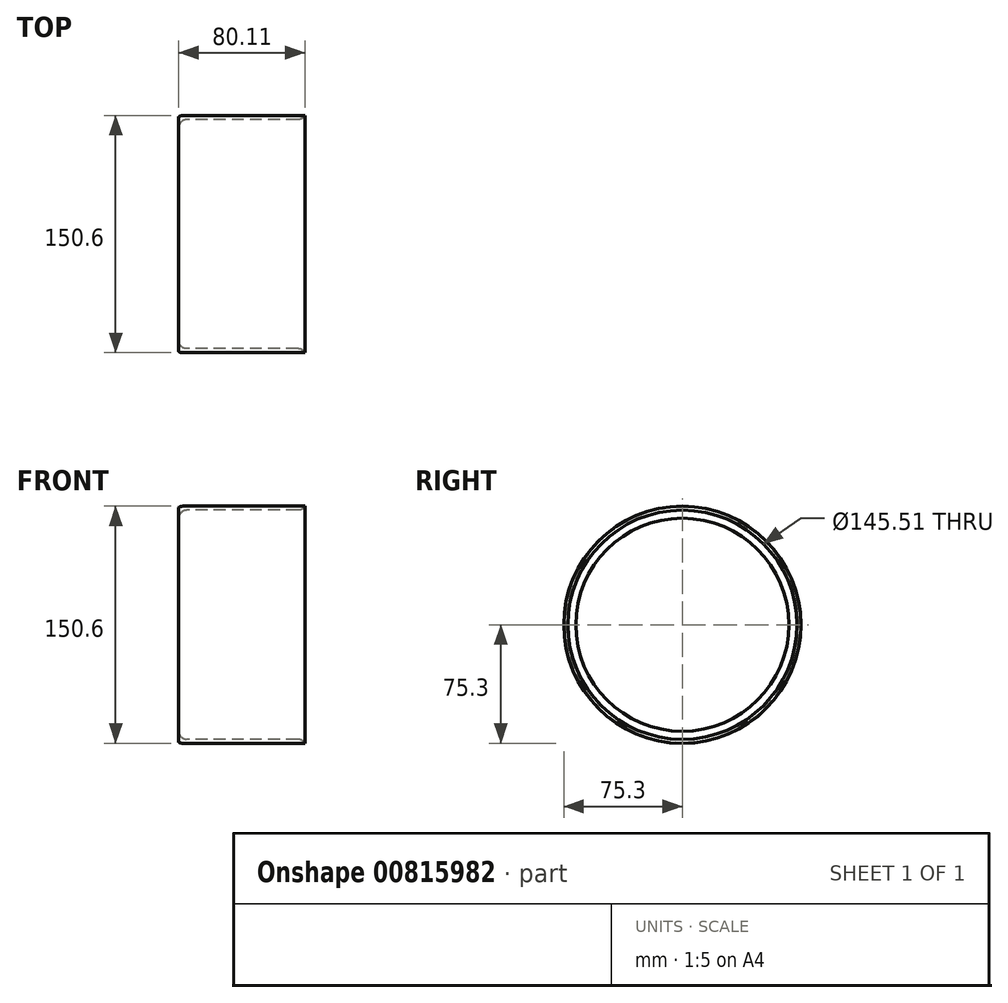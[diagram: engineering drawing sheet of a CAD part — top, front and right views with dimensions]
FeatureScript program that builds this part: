
annotation { "Feature Type Name" : "Feature", "Feature Type Description" : "" }
export const myFeature = defineFeature(function(context is Context, id is Id, definition is map)
    precondition{}
    {
        {
            var Q0;
            Q0=qCreatedBy(makeId("Right.planeOp"),FACE);
            var sketch = newSketch(context, id + "F0", { "sketchPlane" : qUnion([Q0])});
            skCircle(sketch, "E0", {"center": v(0, 0) * mm, "radius": 75.3 * mm});
            skSolve(sketch);
        }
        {
            var Q0;
            Q0=makeQuery(id+"F0.imprint","IMPRINT",FACE,{"disambiguationData":[TD([[makeQuery(id+"F0.imprint","IMPRINT",EDGE,{"derivedFrom":sQuery(id+"F0.wireOp",EDGE,"E0")}),1.0]])]});
            extrude(context, id + "F1", {"entities" : qUnion([Q0]), "depth" : 82.65 * mm, "offsetDistance" : 25.4 * mm});
        }
        {
            var Q0;
            Q0=makeQuery(id+"F1.opExtrude","CAP_FACE",FACE,{"disambiguationData":[OSD([sQuery(id+"F0.wireOp",EDGE,"E0")])],"isStart":false});
            shell(context, id + "F2", {"entities" : qUnion([Q0]), "thickness" : 2.54 * mm});
        }
        {
            var Q0;
            {var subQ0=sQuery(id+"F0.wireOp",EDGE,"E0");Q0=makeQuery(id+"F2.opShell","OFFSET_EDGE",EDGE,{"disambiguationData":[OSD([subQ0]),TDD([makeQuery(id+"F1.opExtrude","CAP_EDGE",EDGE,{"disambiguationData":[OSD([subQ0])],"isStart":false})])]});}
            fillet(context, id + "F3", {"entities" : qUnion([Q0]), "radius" : 5.08 * mm, "tangentPropagation" : true, "allowEdgeOverflow" : false});
        }
        {
            var Q0;
            {var subQ0=sQuery(id+"F0.wireOp",EDGE,"E0");Q0=makeQuery(id+"F2.opShell","OFFSET_FACE",FACE,{"disambiguationData":[OSD([subQ0]),TDD([makeQuery(id+"F1.opExtrude","CAP_FACE",FACE,{"disambiguationData":[OSD([subQ0])],"isStart":true})])]});}
            fillet(context, id + "F4", {"entities" : qUnion([Q0]), "radius" : 5.08 * mm, "tangentPropagation" : true, "allowEdgeOverflow" : false});
        }
        {
            var Q0;
            Q0=makeQuery(id+"F1.opExtrude","CAP_EDGE",EDGE,{"disambiguationData":[OSD([sQuery(id+"F0.wireOp",EDGE,"E0")])],"isStart":true});
            fillet(context, id + "F5", {"entities" : qUnion([Q0]), "radius" : 5.08 * mm, "tangentPropagation" : true, "allowEdgeOverflow" : false});
        }
        {
            var Q0;
            {var subQ0=sQuery(id+"F0.wireOp",EDGE,"E0");Q0=makeQuery(id+"F2.opShell","OFFSET_FACE",FACE,{"disambiguationData":[OSD([subQ0]),TDD([makeQuery(id+"F1.opExtrude","CAP_FACE",FACE,{"disambiguationData":[OSD([subQ0])],"isStart":true})])]});}
            var sketch = newSketch(context, id + "F6", { "sketchPlane" : qUnion([Q0])});
            skPoint(sketch, "E1", {"position": v(0, 0) * mm});
            skSolve(sketch);
        }
        {
            var Q0;
            Q0=sQuery(id+"F6.wireOp",VERTEX,"E1");
            var Q1;
            Q1=makeQuery(id+"F1.opExtrude","SWEPT_BODY",BODY,{"disambiguationData":[OSD([sQuery(id+"F0.wireOp",EDGE,"E0")])]});
            hole(context, id + "F7", {"style" : HoleStyle.SIMPLE, "endStyle" : HoleEndStyle.THROUGH, "holeDiameter" : 635 * mm, "majorDiameter" : 6.35 * mm, "isTappedThrough" : true, "tappedDepth" : 12.7 * mm, "tapClearance" : 3, "locations" : qUnion([Q0]), "scope" : qUnion([Q1])});
        }
    });
